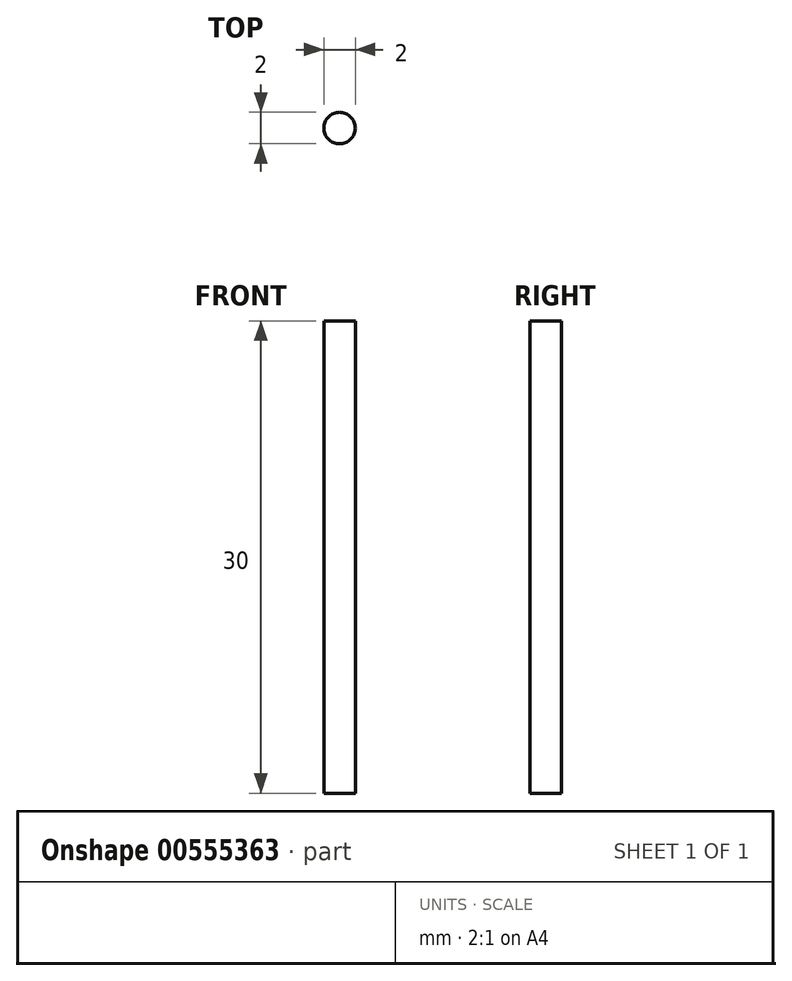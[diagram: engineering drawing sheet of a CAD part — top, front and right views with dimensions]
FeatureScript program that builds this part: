
annotation { "Feature Type Name" : "Feature", "Feature Type Description" : "" }
export const myFeature = defineFeature(function(context is Context, id is Id, definition is map)
    precondition{}
    {
        {
            var Q0;
            Q0=qCreatedBy(makeId("Top.planeOp"),FACE);
            var sketch = newSketch(context, id + "F0", { "sketchPlane" : qUnion([Q0])});
            skCircle(sketch, "E0", {"center": v(0, 0) * mm, "radius": 1 * mm});
            skSolve(sketch);
        }
        {
            var Q0;
            Q0=makeQuery(id+"F0.imprint","IMPRINT",FACE,{"disambiguationData":[TD([[makeQuery(id+"F0.imprint","IMPRINT",EDGE,{"derivedFrom":sQuery(id+"F0.wireOp",EDGE,"E0")}),1.0]])]});
            extrude(context, id + "F1", {"entities" : qUnion([Q0]), "depth" : 30 * mm, "offsetDistance" : 25 * mm});
        }
    });
